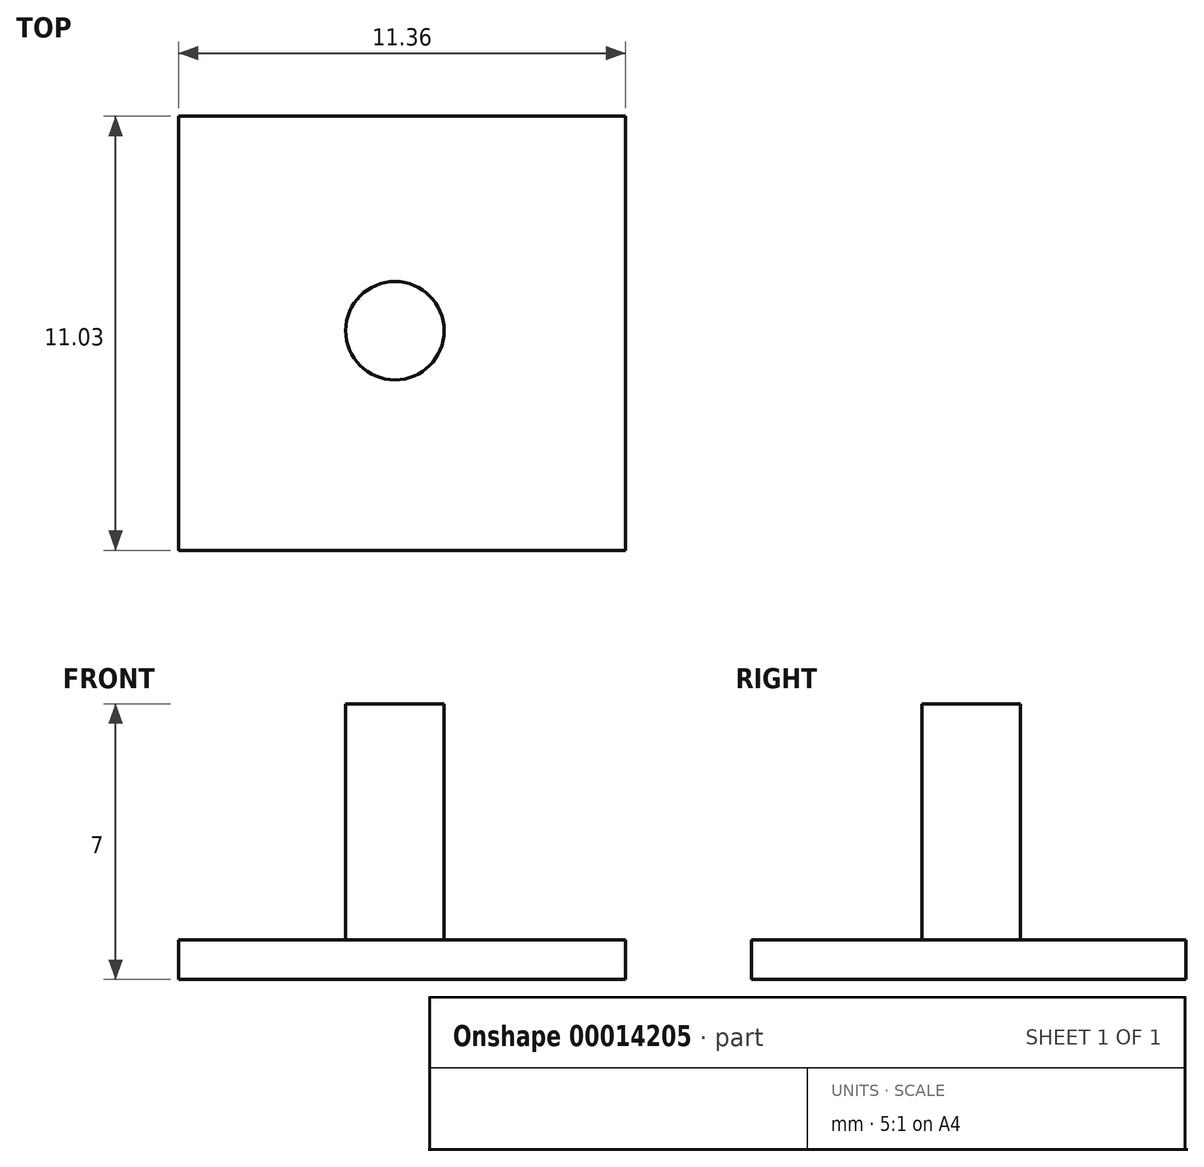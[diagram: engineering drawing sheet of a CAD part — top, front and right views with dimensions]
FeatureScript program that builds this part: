
annotation { "Feature Type Name" : "Feature", "Feature Type Description" : "" }
export const myFeature = defineFeature(function(context is Context, id is Id, definition is map)
    precondition{}
    {
        {
            var Q0;
            Q0=qCreatedBy(makeId("Top.planeOp"),FACE);
            var sketch = newSketch(context, id + "F0", { "sketchPlane" : qUnion([Q0])});
            skLineSegment(sketch, "E0.bottom", {"start": v(-5.5, 5.45) * mm, "end": v(5.86, 5.45) * mm});
            skLineSegment(sketch, "E0.top", {"start": v(-5.5, -5.58) * mm, "end": v(5.86, -5.58) * mm});
            skLineSegment(sketch, "E0.left", {"start": v(-5.5, 5.45) * mm, "end": v(-5.5, -5.58) * mm});
            skLineSegment(sketch, "E0.right", {"start": v(5.86, 5.45) * mm, "end": v(5.86, -5.58) * mm});
            skCircle(sketch, "E1", {"center": v(0, 0) * mm, "radius": 1.25 * mm});
            skSolve(sketch);
        }
        {
            var Q0;
            Q0=makeQuery(id+"F0.imprint","IMPRINT",FACE,{"disambiguationData":[TD([[makeQuery(id+"F0.imprint","IMPRINT",EDGE,{"derivedFrom":sQuery(id+"F0.wireOp",EDGE,"E0.bottom")}),-1.0]])]});
            extrude(context, id + "F1", {"entities" : qUnion([Q0]), "depth" : 1 * mm});
        }
        {
            var Q0;
            Q0=makeQuery(id+"F0.imprint","IMPRINT",FACE,{"disambiguationData":[TD([[makeQuery(id+"F0.imprint","IMPRINT",EDGE,{"derivedFrom":sQuery(id+"F0.wireOp",EDGE,"E1")}),1.0]])]});
            extrude(context, id + "F2", {"entities" : qUnion([Q0]), "operationType" : NewBodyOperationType.ADD, "depth" : 7 * mm});
        }
    });
